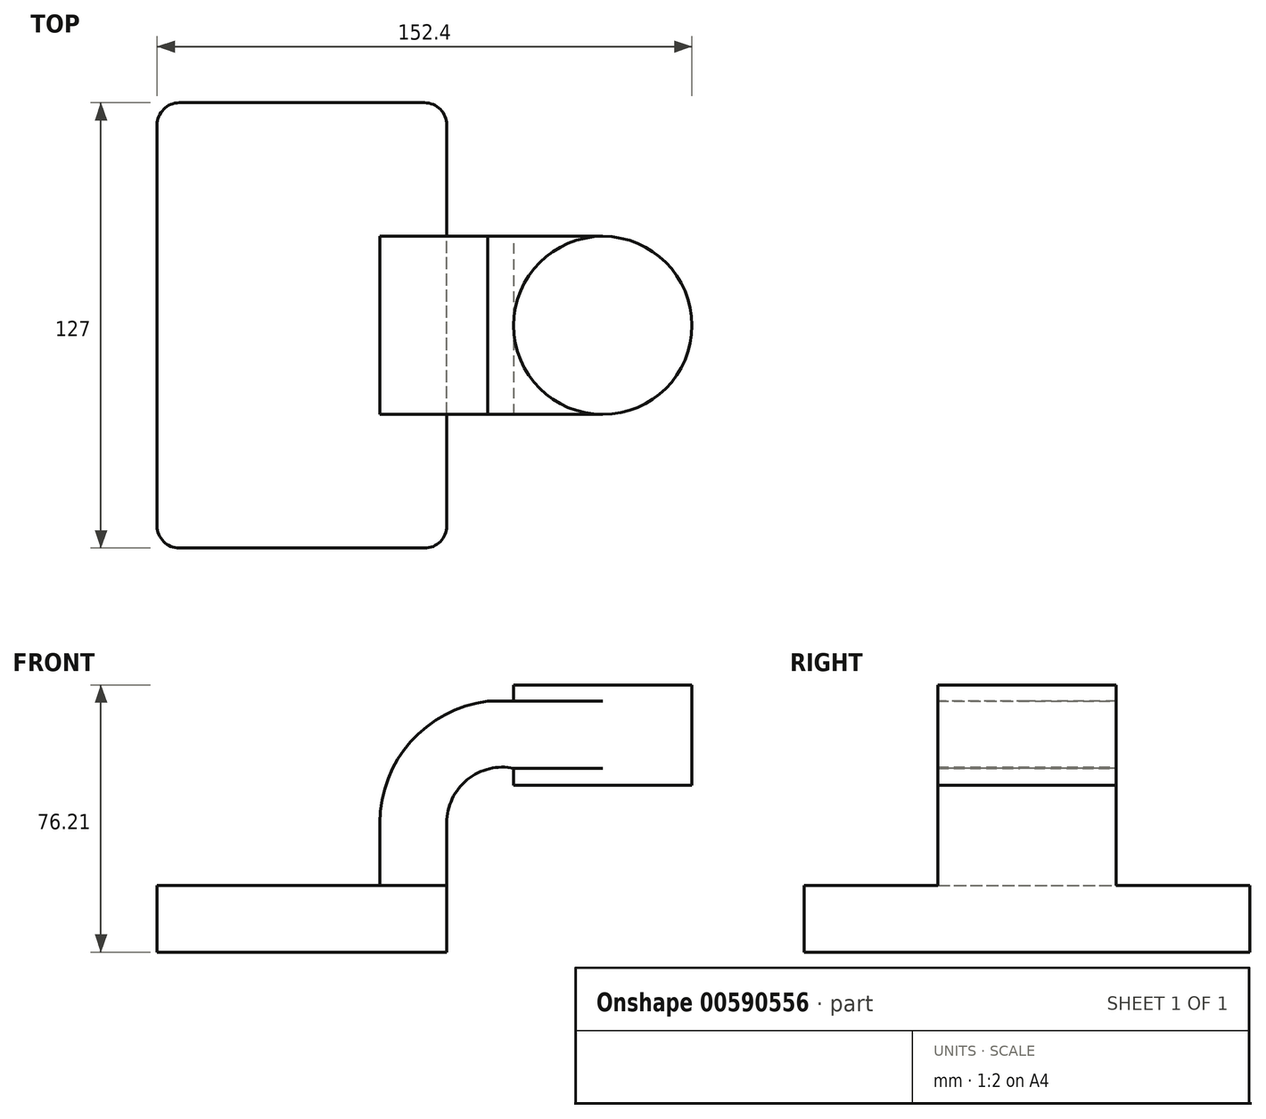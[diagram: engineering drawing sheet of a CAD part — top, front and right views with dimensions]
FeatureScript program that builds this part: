
annotation { "Feature Type Name" : "Feature", "Feature Type Description" : "" }
export const myFeature = defineFeature(function(context is Context, id is Id, definition is map)
    precondition{}
    {
        {
            var Q0;
            Q0=qCreatedBy(makeId("Front.planeOp"),FACE);
            var sketch = newSketch(context, id + "F0", { "sketchPlane" : qUnion([Q0])});
            skLineSegment(sketch, "E0.bottom", {"start": v(-41.28, 9.53) * mm, "end": v(41.28, 9.53) * mm});
            skLineSegment(sketch, "E0.top", {"start": v(-41.28, -9.53) * mm, "end": v(41.28, -9.53) * mm});
            skLineSegment(sketch, "E0.left", {"start": v(-41.28, 9.53) * mm, "end": v(-41.28, -9.53) * mm});
            skLineSegment(sketch, "E0.right", {"start": v(41.28, 9.53) * mm, "end": v(41.28, -9.52) * mm});
            skPoint(sketch, "E0.middle", {"position": v(0, 0) * mm});
            skLineSegment(sketch, "E1.bottom", {"start": v(60.32, 66.67) * mm, "end": v(111.12, 66.67) * mm});
            skLineSegment(sketch, "E1.top", {"start": v(60.32, 38.1) * mm, "end": v(111.12, 38.1) * mm});
            skLineSegment(sketch, "E1.left", {"start": v(60.32, 66.67) * mm, "end": v(60.32, 38.1) * mm});
            skLineSegment(sketch, "E1.right", {"start": v(111.12, 66.67) * mm, "end": v(111.12, 38.1) * mm});
            skPoint(sketch, "E1.middle", {"position": v(85.73, 52.39) * mm});
            skLineSegment(sketch, "E2", {"start": v(41.28, 9.53) * mm, "end": v(41.28, 27.34) * mm});
            skArc(sketch, "E3", {"start": v(41.28, 27.34) * mm, "mid": v(47.14, 39.66) * mm, "end": v(60.4, 42.88) * mm});
            skArc(sketch, "E4.1", {"start": v(22.23, 27.34) * mm, "mid": v(30.99, 50.47) * mm, "end": v(52.88, 62) * mm});
            skLineSegment(sketch, "E4.2", {"start": v(22.23, 9.53) * mm, "end": v(22.23, 27.34) * mm});
            skLineSegment(sketch, "E5", {"start": v(60.4, 42.88) * mm, "end": v(85.73, 42.88) * mm});
            skLineSegment(sketch, "E6", {"start": v(52.88, 62) * mm, "end": v(85.72, 62) * mm});
            skLineSegment(sketch, "E7", {"start": v(85.72, 38.1) * mm, "end": v(85.72, 66.67) * mm});
            skFitSpline(sketch, "E8", {"points": [v(-41.28, 9.52) * mm, v(52.88, 62) * mm], "startDerivative": vector(0, 55.14) * mm, "endDerivative": vector(91.95, 0) * mm});
            skSolve(sketch);
        }
        {
            var Q0;
            Q0=makeQuery(id+"F0.imprint","IMPRINT",FACE,{"disambiguationData":[TD([[makeQuery(id+"F0.imprint","IMPRINT",EDGE,{"derivedFrom":sQuery(id+"F0.wireOp",EDGE,"E0.top")}),1.0]])]});
            extrude(context, id + "F1", {"entities" : qUnion([Q0]), "endBound" : BoundingType.SYMMETRIC, "depth" : 127 * mm, "offsetDistance" : 25.4 * mm});
        }
        {
            var Q0;
            {var subQ1=sQuery(id+"F0.wireOp",EDGE,"E2");Q0=makeQuery(id+"F0.imprint","IMPRINT",FACE,{"disambiguationData":[TD([[makeQuery(id+"F0.imprint","IMPRINT",EDGE,{"derivedFrom":subQ1}),1.0]])]});}
            var Q1;
            {var subQ0=sQuery(id+"F0.wireOp",EDGE,"E5");Q1=makeQuery(id+"F0.imprint","IMPRINT",FACE,{"disambiguationData":[TD([[makeQuery(id+"F0.imprint","IMPRINT",EDGE,{"derivedFrom":subQ0}),1.0]])]});}
            extrude(context, id + "F2", {"entities" : qUnion([Q0, Q1]), "operationType" : NewBodyOperationType.ADD, "endBound" : BoundingType.SYMMETRIC, "depth" : 50.8 * mm, "offsetDistance" : 25.4 * mm});
        }
        {
            var Q0;
            Q0=makeQuery(id+"F0.imprint","IMPRINT",FACE,{"disambiguationData":[TD([[makeQuery(id+"F0.imprint","IMPRINT",EDGE,{"derivedFrom":sQuery(id+"F0.wireOp",EDGE,"E4.1")}),1.0]])]});
            extrude(context, id + "F3", {"entities" : qUnion([Q0]), "operationType" : NewBodyOperationType.ADD, "endBound" : BoundingType.SYMMETRIC, "depth" : 15.88 * mm, "offsetDistance" : 25.4 * mm});
        }
        {
            var Q0;
            {var subQ0=sQuery(id+"F0.wireOp",EDGE,"E1.right");Q0=makeQuery(id+"F0.imprint","IMPRINT",FACE,{"disambiguationData":[TD([[makeQuery(id+"F0.imprint","IMPRINT",EDGE,{"derivedFrom":subQ0}),-1.0]])]});}
            var Q1;
            Q1=sQuery(id+"F0.wireOp",EDGE,"E7");
            revolve(context, id + "F4", {"operationType" : NewBodyOperationType.ADD, "entities" : qUnion([Q0]), "axis" : qUnion([Q1]), "revolveType" : RevolveType.FULL});
        }
        {
            var Q0;
            Q0=makeQuery(id+"F1.opExtrude","CAP_EDGE",EDGE,{"disambiguationData":[OSD([sQuery(id+"F0.wireOp",EDGE,"E0.right")])],"isStart":false});
            var Q1;
            Q1=makeQuery(id+"F1.opExtrude","CAP_EDGE",EDGE,{"disambiguationData":[OSD([sQuery(id+"F0.wireOp",EDGE,"E0.right")])],"isStart":true});
            var Q2;
            Q2=makeQuery(id+"F1.opExtrude","CAP_EDGE",EDGE,{"disambiguationData":[OSD([sQuery(id+"F0.wireOp",EDGE,"E0.left")])],"isStart":true});
            var Q3;
            Q3=makeQuery(id+"F1.opExtrude","CAP_EDGE",EDGE,{"disambiguationData":[OSD([sQuery(id+"F0.wireOp",EDGE,"E0.left")])],"isStart":false});
            fillet(context, id + "F5", {"entities" : qUnion([Q0, Q1, Q2, Q3]), "radius" : 6.35 * mm, "tangentPropagation" : true, "allowEdgeOverflow" : false});
        }
    });
